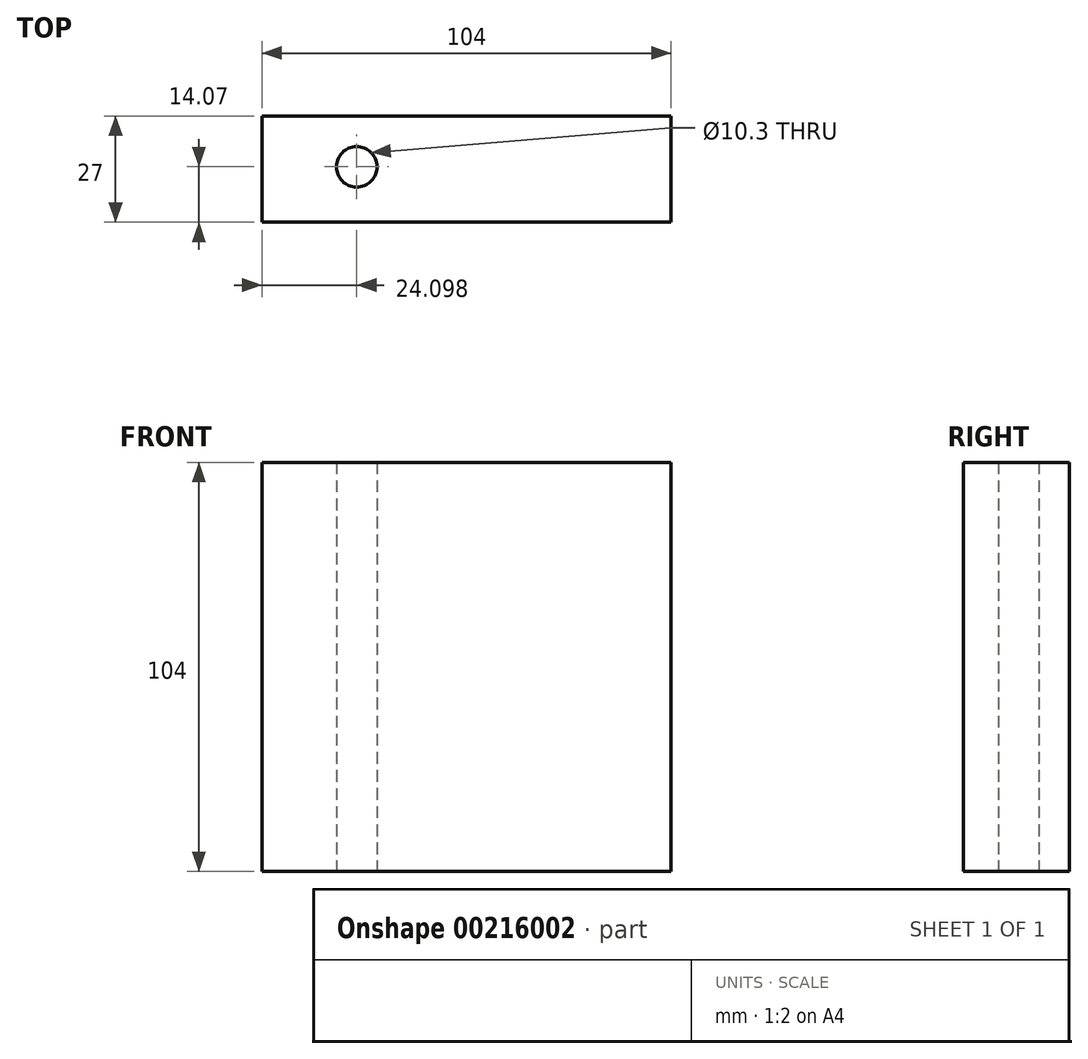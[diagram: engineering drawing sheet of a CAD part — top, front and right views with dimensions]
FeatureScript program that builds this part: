
annotation { "Feature Type Name" : "Feature", "Feature Type Description" : "" }
export const myFeature = defineFeature(function(context is Context, id is Id, definition is map)
    precondition{}
    {
        {
            var Q0;
            Q0=qCreatedBy(makeId("Front.planeOp"),FACE);
            var sketch = newSketch(context, id + "F0", { "sketchPlane" : qUnion([Q0])});
            skLineSegment(sketch, "E0.bottom", {"start": v(-52, 52) * mm, "end": v(52, 52) * mm});
            skLineSegment(sketch, "E0.top", {"start": v(-52, -52) * mm, "end": v(52, -52) * mm});
            skLineSegment(sketch, "E0.left", {"start": v(-52, 52) * mm, "end": v(-52, -52) * mm});
            skLineSegment(sketch, "E0.right", {"start": v(52, 52) * mm, "end": v(52, -52) * mm});
            skSolve(sketch);
        }
        {
            var Q0;
            Q0 = qSketchRegion(id + "F0", true);
            extrude(context, id + "F1", {"entities" : qUnion([Q0]), "depth" : 27 * mm});
        }
        {
            var Q0;
            Q0=makeQuery(id+"F1.opExtrude","SWEPT_FACE",FACE,{"disambiguationData":[OSD([sQuery(id+"F0.wireOp",EDGE,"E0.top")])]});
            var sketch = newSketch(context, id + "F2", { "sketchPlane" : qUnion([Q0])});
            skPoint(sketch, "E1", {"position": v(-27.9, 12.93) * mm});
            skSolve(sketch);
        }
        {
            var Q0;
            Q0=sQuery(id+"F2.wireOp",VERTEX,"E1");
            var Q1;
            Q1=makeQuery(id+"F1.opExtrude","SWEPT_BODY",BODY,{"disambiguationData":[OSD([sQuery(id+"F0.wireOp",EDGE,"E0.bottom"),sQuery(id+"F0.wireOp",EDGE,"E0.top"),sQuery(id+"F0.wireOp",EDGE,"E0.left"),sQuery(id+"F0.wireOp",EDGE,"E0.right")])]});
            hole(context, id + "F3", {"style" : HoleStyle.SIMPLE, "endStyle" : HoleEndStyle.THROUGH, "standardTappedOrClearance" : lookupTablePath({ "standard" : "ISO", "engagement" : "75%", "pitch" : "1.75 mm", "size" : "M12", "type" : "Tapped" }), "standardBlindInLast" : lookupTablePath({ "standard" : "ISO", "engagement" : "75%", "pitch" : "1.75 mm", "size" : "M12", "type" : "Tapped" }), "holeDiameter" : 10.3 * mm, "locations" : qUnion([Q0]), "scope" : qUnion([Q1]), "isTappedThrough" : true, "majorDiameter" : 12 * mm, "showTappedDepth" : true});
        }
    });
